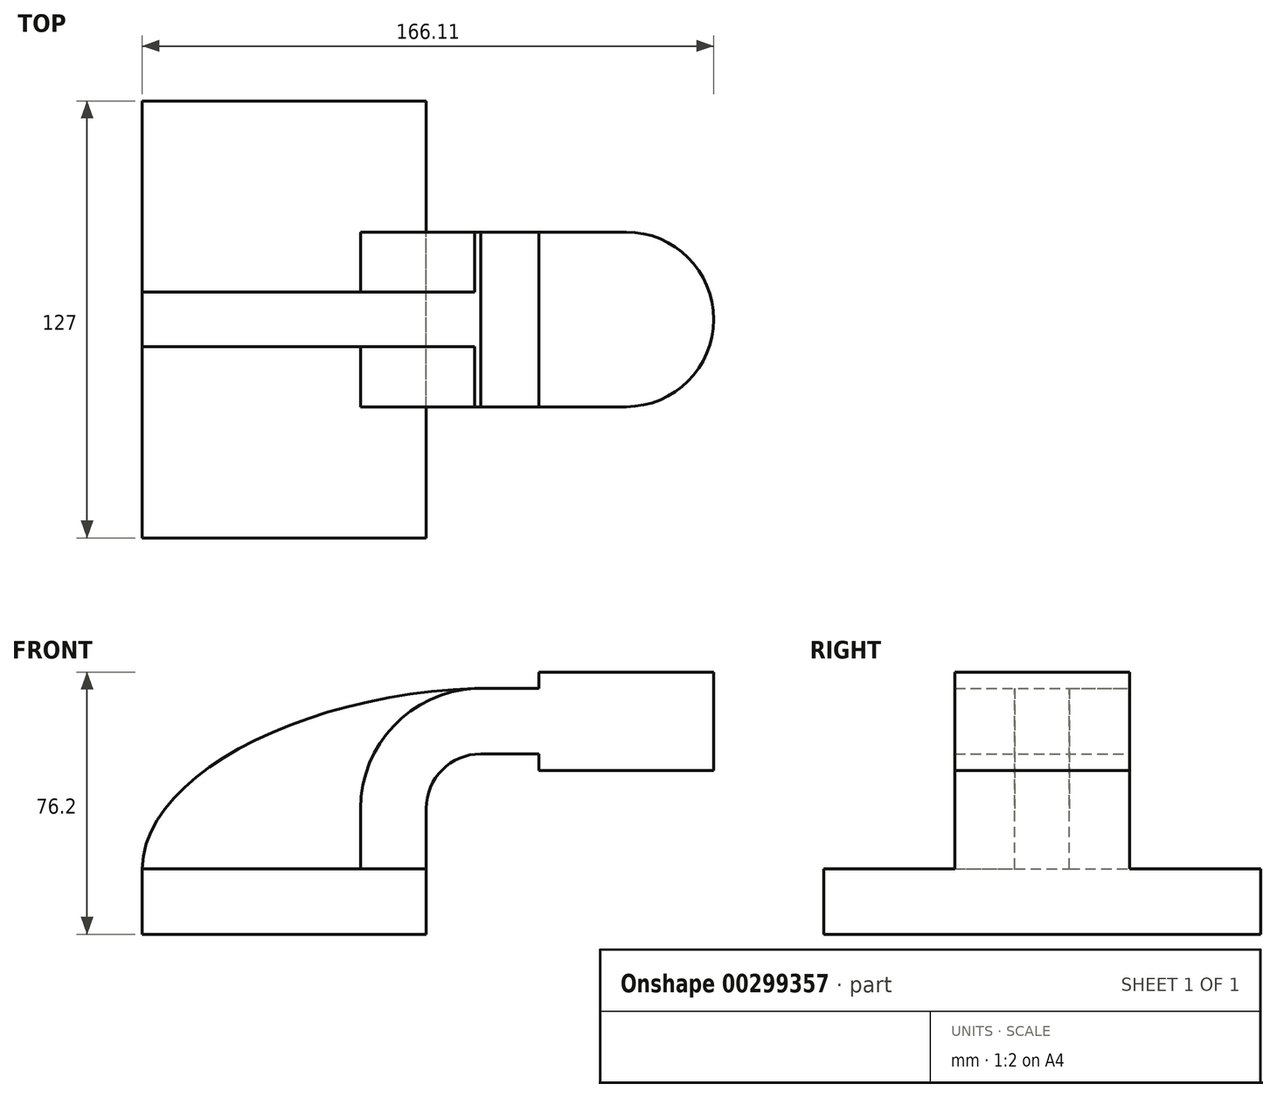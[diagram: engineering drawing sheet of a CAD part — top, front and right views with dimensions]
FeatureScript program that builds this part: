
annotation { "Feature Type Name" : "Feature", "Feature Type Description" : "" }
export const myFeature = defineFeature(function(context is Context, id is Id, definition is map)
    precondition{}
    {
        {
            var Q0;
            Q0=qCreatedBy(makeId("Front.planeOp"),FACE);
            var sketch = newSketch(context, id + "F0", { "sketchPlane" : qUnion([Q0])});
            skLineSegment(sketch, "E0.bottom", {"start": v(-41.28, 9.52) * mm, "end": v(41.27, 9.53) * mm});
            skLineSegment(sketch, "E0.top", {"start": v(-41.28, -9.53) * mm, "end": v(41.28, -9.53) * mm});
            skLineSegment(sketch, "E0.left", {"start": v(-41.28, 9.52) * mm, "end": v(-41.27, -9.53) * mm});
            skLineSegment(sketch, "E0.right", {"start": v(41.28, 9.53) * mm, "end": v(41.28, -9.52) * mm});
            skPoint(sketch, "E0.middle", {"position": v(0, 0) * mm});
            skLineSegment(sketch, "E1", {"start": v(41.27, 9.53) * mm, "end": v(41.27, 27) * mm});
            skArc(sketch, "E2", {"start": v(41.27, 27) * mm, "mid": v(45.92, 38.23) * mm, "end": v(57.15, 42.88) * mm});
            skLineSegment(sketch, "E3", {"start": v(57.15, 42.88) * mm, "end": v(99.43, 42.88) * mm});
            skLineSegment(sketch, "E4.bottom", {"start": v(74.03, 66.67) * mm, "end": v(124.83, 66.67) * mm});
            skLineSegment(sketch, "E4.top", {"start": v(74.03, 38.1) * mm, "end": v(124.83, 38.1) * mm});
            skLineSegment(sketch, "E4.left", {"start": v(74.03, 66.67) * mm, "end": v(74.03, 38.1) * mm});
            skLineSegment(sketch, "E4.right", {"start": v(124.83, 66.67) * mm, "end": v(124.83, 38.1) * mm});
            skPoint(sketch, "E4.middle", {"position": v(99.43, 52.39) * mm});
            skLineSegment(sketch, "E5.0", {"start": v(57.15, 61.93) * mm, "end": v(99.43, 61.93) * mm});
            skArc(sketch, "E5.1", {"start": v(22.22, 27) * mm, "mid": v(32.45, 51.7) * mm, "end": v(57.15, 61.93) * mm});
            skLineSegment(sketch, "E5.2", {"start": v(22.22, 9.53) * mm, "end": v(22.22, 27) * mm});
            skFitSpline(sketch, "E6", {"points": [v(-41.28, 9.52) * mm, v(57.15, 61.93) * mm], "startDerivative": vector(1.44, 84.62) * mm, "endDerivative": vector(146.4, 2.93) * mm});
            skLineSegment(sketch, "E7", {"start": v(99.43, 38.1) * mm, "end": v(99.43, 66.67) * mm});
            skLineSegment(sketch, "E8.bottom", {"start": v(74.03, 66.67) * mm, "end": v(99.43, 66.67) * mm});
            skLineSegment(sketch, "E8.top", {"start": v(74.03, 61.93) * mm, "end": v(99.43, 61.93) * mm});
            skLineSegment(sketch, "E8.left", {"start": v(74.03, 66.67) * mm, "end": v(74.03, 61.93) * mm});
            skLineSegment(sketch, "E8.right", {"start": v(99.43, 66.67) * mm, "end": v(99.43, 61.93) * mm});
            skLineSegment(sketch, "E9.bottom", {"start": v(99.43, 42.88) * mm, "end": v(74.03, 42.88) * mm});
            skLineSegment(sketch, "E9.top", {"start": v(99.43, 38.1) * mm, "end": v(74.03, 38.1) * mm});
            skLineSegment(sketch, "E9.left", {"start": v(99.43, 42.88) * mm, "end": v(99.43, 38.1) * mm});
            skLineSegment(sketch, "E9.right", {"start": v(74.03, 42.88) * mm, "end": v(74.03, 38.1) * mm});
            skLineSegment(sketch, "E10.bottom", {"start": v(74.03, 42.88) * mm, "end": v(99.43, 42.88) * mm});
            skLineSegment(sketch, "E10.top", {"start": v(74.03, 38.1) * mm, "end": v(99.43, 38.1) * mm});
            skSolve(sketch);
        }
        {
            var Q0;
            Q0=makeQuery(id+"F0.imprint","IMPRINT",FACE,{"disambiguationData":[TD([[makeQuery(id+"F0.imprint","IMPRINT",EDGE,{"derivedFrom":sQuery(id+"F0.wireOp",EDGE,"E0.top")}),1.0]])]});
            extrude(context, id + "F1", {"entities" : qUnion([Q0]), "endBound" : BoundingType.SYMMETRIC, "depth" : 127 * mm});
        }
        {
            var Q0;
            {var subQ4=sQuery(id+"F0.wireOp",EDGE,"E1");Q0=makeQuery(id+"F0.imprint","IMPRINT",FACE,{"disambiguationData":[TD([[makeQuery(id+"F0.imprint","IMPRINT",EDGE,{"derivedFrom":subQ4}),1.0]])]});}
            var Q1;
            {var subQ0=sQuery(id+"F0.wireOp",EDGE,"E7");var subQ1=sQuery(id+"F0.wireOp",EDGE,"E3");var subQ2=makeQuery(id+"F0.imprint","INTERSECT",VERTEX,{"derivedFrom":[subQ1,subQ0]});Q1=makeQuery(id+"F0.imprint","IMPRINT",FACE,{"disambiguationData":[TD([[makeQuery(id+"F0.imprint","IMPRINT",EDGE,{"disambiguationData":[TD([[subQ2,1.0]])],"derivedFrom":subQ1}),1.0]])]});}
            var Q2;
            Q2=makeQuery(id+"F0.imprint","IMPRINT",FACE,{"disambiguationData":[TD([[makeQuery(id+"F0.imprint","IMPRINT",EDGE,{"derivedFrom":sQuery(id+"F0.wireOp",EDGE,"E7")}),1.0]])]});
            extrude(context, id + "F2", {"entities" : qUnion([Q0, Q1, Q2]), "operationType" : NewBodyOperationType.ADD, "endBound" : BoundingType.SYMMETRIC, "depth" : 50.8 * mm});
        }
        {
            var Q0;
            {var subQ3=sQuery(id+"F0.wireOp",EDGE,"E5.2");Q0=makeQuery(id+"F0.imprint","IMPRINT",FACE,{"disambiguationData":[TD([[makeQuery(id+"F0.imprint","IMPRINT",EDGE,{"derivedFrom":subQ3}),1.0]])]});}
            extrude(context, id + "F3", {"entities" : qUnion([Q0]), "operationType" : NewBodyOperationType.ADD, "endBound" : BoundingType.SYMMETRIC, "depth" : 15.88 * mm});
        }
        {
            var Q0;
            Q0=makeQuery(id+"F0.imprint","IMPRINT",FACE,{"disambiguationData":[TD([[makeQuery(id+"F0.imprint","IMPRINT",EDGE,{"derivedFrom":sQuery(id+"F0.wireOp",EDGE,"E7")}),-1.0]])]});
            var Q1;
            Q1=sQuery(id+"F0.wireOp",EDGE,"E7");
            revolve(context, id + "F4", {"operationType" : NewBodyOperationType.ADD, "entities" : qUnion([Q0]), "axis" : qUnion([Q1]), "revolveType" : RevolveType.FULL});
        }
    });
